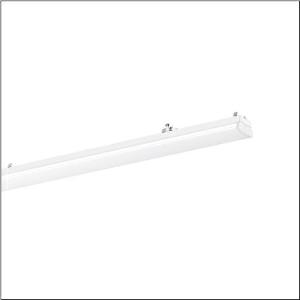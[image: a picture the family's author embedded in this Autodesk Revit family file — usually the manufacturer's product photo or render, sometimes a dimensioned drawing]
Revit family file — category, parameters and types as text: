
# Revit family: licross_r__21_recessed_opal_mo_52tl1d7n48xg_bf27
name_source: partatom
category: Lighting Fixtures
units: mm (PartAtom-declared; Revit-internal decimal feet)

## family parameters
Cut with Voids When Loaded = No
Host = Face
Light Source = No
Part Type = Normal
Room Calculation Point = No
Round Connector Dimension = Use Diameter
Shared = No

## types (1)
- Licross® 21 recessed opal MO (1 x LED, 8360 lm, 47.9 W, 4000K)
    Apparent Load = 48 VA
    CIE Flux Codes = 44 73 91 87 100
    Color Rendering = 80
    Color Temperature = 4000K
    Default Elevation = 1800 mm
    Description = Licross® 21 recessed opal MO, luminaire insert, of sheet steel, galvanised, coil coated, white, length: 1.500mm, width: 66mm, height: 67mm, LED rated luminous flux: 8.360lm, light colour: 840, control gear: ON/OFF, with plug, 3-pole, with phase selection, mains connection: 220..240V, AC, 50/60Hz, rated input power: 48W, halogen-free wiring, primary optical cover: cover, of PMMA, light emission: direct with ceiling illumination distribution, primary light characteristic: symmetric, protection rating (complete): IP40, insulation class (complete): insulation class I (protective earthing), certification: CE, ENEC, VDE, UKCA, protection symbol: D if used in an environment without relevant dust loads with corresponding accessories, impact resistance: IK06, permissible ambient temperature for indoor applications: -35..+40°C, corresponds to IFS (International Featured Standards) requirements for safety and quality in the food industry, reducing of maximum allowable ambient temperature of 5°C with ceiling mounting, LABS conformity tested according to VDMA 24364:2018-05, packaging unit: 1 piece
    Height = 83 mm
    Lamp = 1 x LED
    Lamp Light Flux = 8360 lm
    Lamp Power = 47.9 W
    Lamp count = 1
    Length = 1500 mm
    Luminous efficacy = 175 lm/W
    Manufacturer = Siteco
    ModVariant = No
    Model = 52TL1D7N48XG
    Mounting Place = Ceiling
    Mounting Type = Pendant
    Number of Poles = 1
    OnlyDefault = Yes
    Power Factor = 1
    Product Name = Licross® 21 recessed opal MO
    Product group = luminaire insert
    ProductGroupID = 901
    Protection Class = Protection class I
    Protection Degree = IP 40
    RLX_Detail_Level = 1
    RLX_Emergency_Light_Flux = 0 lm
    RLX_Emergency_Type = 0
    RLX_Emergency_Type_DB = No
    RlxData = <blob elided: 23121 chars, md5=1c1c4442>
    Socket = socket
    Standby Power = 0 W
    System Light Flux = 8360 lm
    System Power = 48 W
    Type Comments = Product without accessories
    Type Image = l_1313666.jpg
    URL = http://relux.com
    VarID = ---
    Voltage = 0 V
    Weight = 0.00 kg
    Width = 76 mm

## geometry (parser evidence)
native form markers: Blend x4, Sweep x13
no freeform markers — native parametric forms only
